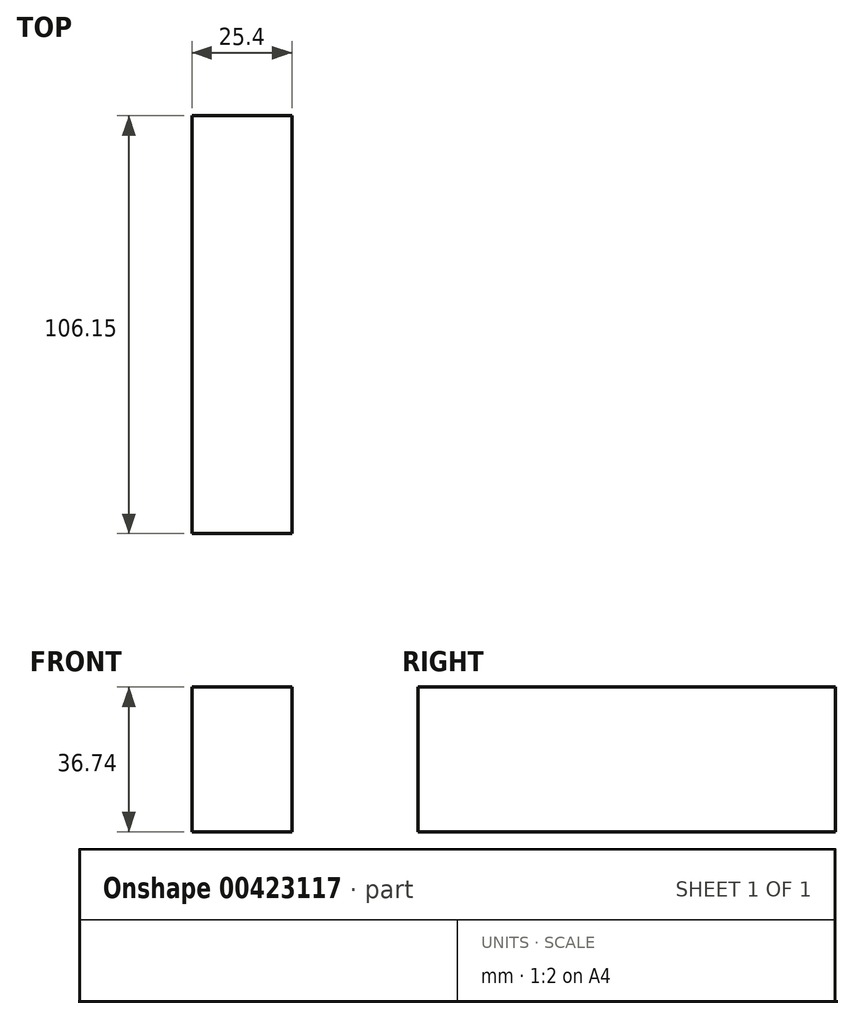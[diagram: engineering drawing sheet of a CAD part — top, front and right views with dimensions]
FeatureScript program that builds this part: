
annotation { "Feature Type Name" : "Feature", "Feature Type Description" : "" }
export const myFeature = defineFeature(function(context is Context, id is Id, definition is map)
    precondition{}
    {
        {
            var Q0;
            Q0=qCreatedBy(makeId("Right.planeOp"),FACE);
            var sketch = newSketch(context, id + "F0", { "sketchPlane" : qUnion([Q0])});
            skLineSegment(sketch, "E0.bottom", {"start": v(43.3, 0) * mm, "end": v(-62.84, 0) * mm});
            skLineSegment(sketch, "E0.top", {"start": v(43.3, 36.74) * mm, "end": v(-62.84, 36.74) * mm});
            skLineSegment(sketch, "E0.left", {"start": v(43.3, 0) * mm, "end": v(43.3, 36.74) * mm});
            skLineSegment(sketch, "E0.right", {"start": v(-62.84, 0) * mm, "end": v(-62.84, 36.74) * mm});
            skSolve(sketch);
        }
        {
            var Q0;
            Q0 = qSketchRegion(id + "F0", true);
            extrude(context, id + "F1", {"entities" : qUnion([Q0]), "depth" : 25.4 * mm});
        }
    });
